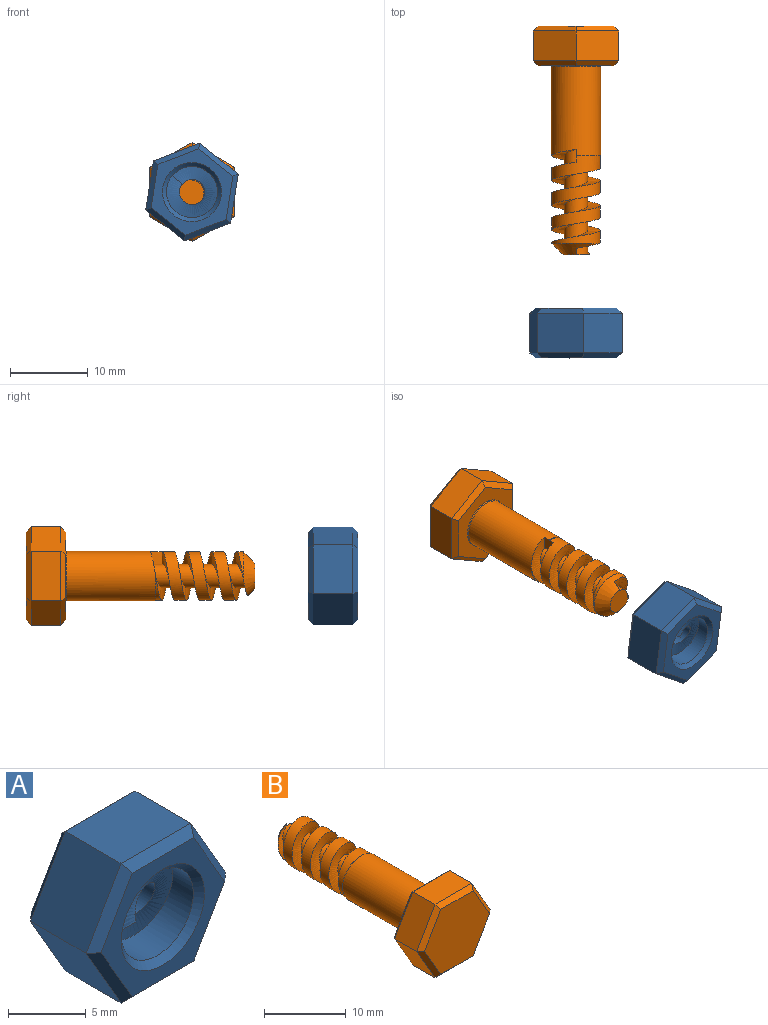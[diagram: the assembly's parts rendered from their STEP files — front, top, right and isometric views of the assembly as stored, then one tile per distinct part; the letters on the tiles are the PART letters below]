
ASSEMBLY  parts=2 mates=1
PART A: 28 faces, bbox 12.7x6.4x11 mm
  f0: cylinder r=1.63mm len=4.67mm, axis (0,1,0), area 15.3mm2, adj f1,f11,f24,f25
  f1: bspline ~7.57x6.55mm, area 26mm2, adj f0,f10,f24,f25
  f2: plane 11.23x9.73mm, normal (0,-1,0), area 37mm2, adj f18,f19,f20,f21,f22,f23,f27
  f3: plane 6.35x5.08mm, normal (0,0,1), area 32.3mm2, adj f4,f8,f17,f19
  f4: plane 5.5x5.08mm, normal (-0.87,0,0.5), area 32.3mm2, adj f3,f5,f15,f18
  f5: plane 5.5x5.08mm, normal (-0.87,0,-0.5), area 32.3mm2, adj f4,f6,f13,f20
  f6: plane 6.35x5.08mm, normal (0,0,-1), area 32.3mm2, adj f5,f7,f12,f22
  f7: plane 5.5x5.08mm, normal (0.87,0,-0.5), area 32.3mm2, adj f6,f8,f14,f23
  f8: plane 5.5x5.08mm, normal (0.87,0,0.5), area 32.3mm2, adj f3,f7,f16,f21
  f9: plane 11.23x9.73mm, normal (0,1,0), area 37mm2, adj f12,f13,f14,f15,f16,f17,f26
  f10: cylinder r=3.28mm len=6.55mm, axis (0,1,0), area 79mm2, adj f1,f11,f24,f25,f26,f27
  f11: bspline ~7.57x6.55mm, area 26mm2, adj f0,f10,f24,f25
  f12: plane 6.35x0.64mm, normal (0,0.71,-0.71), area 5.4mm2, adj f6,f9,f13,f14
  f13: plane 5.5x3.54mm, normal (-0.61,0.71,-0.35), area 5.4mm2, adj f5,f9,f12,f15
  f14: plane 5.5x3.54mm, normal (0.61,0.71,-0.35), area 5.4mm2, adj f7,f9,f12,f16
  f15: plane 5.5x3.54mm, normal (-0.61,0.71,0.35), area 5.4mm2, adj f4,f9,f13,f17
  f16: plane 5.5x3.54mm, normal (0.61,0.71,0.35), area 5.4mm2, adj f8,f9,f14,f17
  f17: plane 6.35x0.64mm, normal (0,0.71,0.71), area 5.4mm2, adj f3,f9,f15,f16
  f18: plane 5.5x3.54mm, normal (-0.61,-0.71,0.35), area 5.4mm2, adj f2,f4,f19,f20
  f19: plane 6.35x0.64mm, normal (0,-0.71,0.71), area 5.4mm2, adj f2,f3,f18,f21
  f20: plane 5.5x3.54mm, normal (-0.61,-0.71,-0.35), area 5.4mm2, adj f2,f5,f18,f22
  f21: plane 5.5x3.54mm, normal (0.61,-0.71,0.35), area 5.4mm2, adj f2,f8,f19,f23
  f22: plane 6.35x0.64mm, normal (0,-0.71,-0.71), area 5.4mm2, adj f2,f6,f20,f23
  f23: plane 5.5x3.54mm, normal (0.61,-0.71,-0.35), area 5.4mm2, adj f2,f7,f21,f22
  f24: plane 1.65x1.5mm, normal (0,0,-1), area 2.5mm2, adj f0,f1,f10,f11
  f25: plane 1.65x1.5mm, normal (0,0,1), area 2.5mm2, adj f0,f1,f10,f11
  f26: cone r=3.78mm half-angle=45deg, axis (0,1,0), area 15.9mm2, adj f9,f10
  f27: cone r=3.28mm half-angle=45deg, axis (0,-1,0), area 15.9mm2, adj f2,f10
PART B: 31 faces, bbox 12.7x29.6x11 mm
  f0: cylinder r=3.11mm len=11.24mm, axis (0,-1,0), area 107.6mm2, adj f9,f12,f14,f16,f18
  f1: plane 6.35x3.81mm, normal (0,0,1), area 24.2mm2, adj f2,f6,f19,f30
  f2: plane 5.5x3.81mm, normal (-0.87,0,0.5), area 24.2mm2, adj f1,f3,f21,f28
  f3: plane 5.5x3.81mm, normal (-0.87,0,-0.5), area 24.2mm2, adj f2,f4,f23,f26
  f4: plane 6.35x3.81mm, normal (0,0,-1), area 24.2mm2, adj f3,f5,f24,f25
  f5: plane 5.5x3.81mm, normal (0.87,0,-0.5), area 24.2mm2, adj f4,f6,f22,f27
  f6: plane 5.5x3.81mm, normal (0.87,0,0.5), area 24.2mm2, adj f1,f5,f20,f29
  f7: plane 11.23x9.73mm, normal (0,-1,0), area 82mm2, adj f25,f26,f27,f28,f29,f30
  f8: plane 11.23x9.73mm, normal (0,1,0), area 48.3mm2, adj f11,f19,f20,f21,f22,f23,f24
  f9: plane 6.35x6.34mm, normal (0,1,0), area 0.9mm2, adj f0,f10,f14,f18
  f10: cylinder r=3.17mm len=11.43mm, axis (0,-1,0), area 225.9mm2, adj f9,f11,f14,f18
  f11: torus R=3.31mm, axis (0,-1,0), area 3.5mm2, adj f8,f10
  f12: cone r=3.37mm half-angle=45deg, axis (0,-1,0), area 16.7mm2, adj f0,f13,f15,f16,f18
  f13: plane 3.31x3.31mm, normal (0,1,0), area 8.2mm2, adj f12,f15,f16,f17
  f14: plane 1.68x1.65mm, normal (0,0,-1), area 2.7mm2, adj f0,f9,f10,f16,f17,f18
  f15: plane 0.98x0.83mm, normal (0,0,1), area 0.5mm2, adj f12,f13,f17,f18
  f16: bspline ~12.17x7.57mm, area 84mm2, adj f0,f12,f13,f14,f17
  f17: cylinder r=1.5mm len=13.53mm, axis (0,-1,0), area 61mm2, adj f13,f14,f15,f16,f18
  f18: bspline ~12.7x7.57mm, area 94.9mm2, adj f0,f9,f10,f12,f14,f15,f17
  f19: plane 6.35x0.64mm, normal (0,0.71,0.71), area 5.4mm2, adj f1,f8,f20,f21
  f20: plane 5.5x3.54mm, normal (0.61,0.71,0.35), area 5.4mm2, adj f6,f8,f19,f22
  f21: plane 5.5x3.54mm, normal (-0.61,0.71,0.35), area 5.4mm2, adj f2,f8,f19,f23
  f22: plane 5.5x3.54mm, normal (0.61,0.71,-0.35), area 5.4mm2, adj f5,f8,f20,f24
  f23: plane 5.5x3.54mm, normal (-0.61,0.71,-0.35), area 5.4mm2, adj f3,f8,f21,f24
  f24: plane 6.35x0.64mm, normal (0,0.71,-0.71), area 5.4mm2, adj f4,f8,f22,f23
  f25: plane 6.35x0.64mm, normal (0,-0.71,-0.71), area 5.4mm2, adj f4,f7,f26,f27
  f26: plane 5.5x3.54mm, normal (-0.61,-0.71,-0.35), area 5.4mm2, adj f3,f7,f25,f28
  f27: plane 5.5x3.54mm, normal (0.61,-0.71,-0.35), area 5.4mm2, adj f5,f7,f25,f29
  f28: plane 5.5x3.54mm, normal (-0.61,-0.71,0.35), area 5.4mm2, adj f2,f7,f26,f30
  f29: plane 5.5x3.54mm, normal (0.61,-0.71,0.35), area 5.4mm2, adj f6,f7,f27,f30
  f30: plane 6.35x0.64mm, normal (0,-0.71,0.71), area 5.4mm2, adj f1,f7,f28,f29
PLACE A rot(axis=(0,1,0),38.8deg) t=(-10.23,-3.81,23.29)mm
PLACE B rot(axis=(0.71,0,0.71),180deg) t=(-10.23,27.31,23.29)mm fixed
MATE cylindrical B.f10 <-> A.f0  axis (0,-1,0) through (-10.23,3.05,23.29)mm
